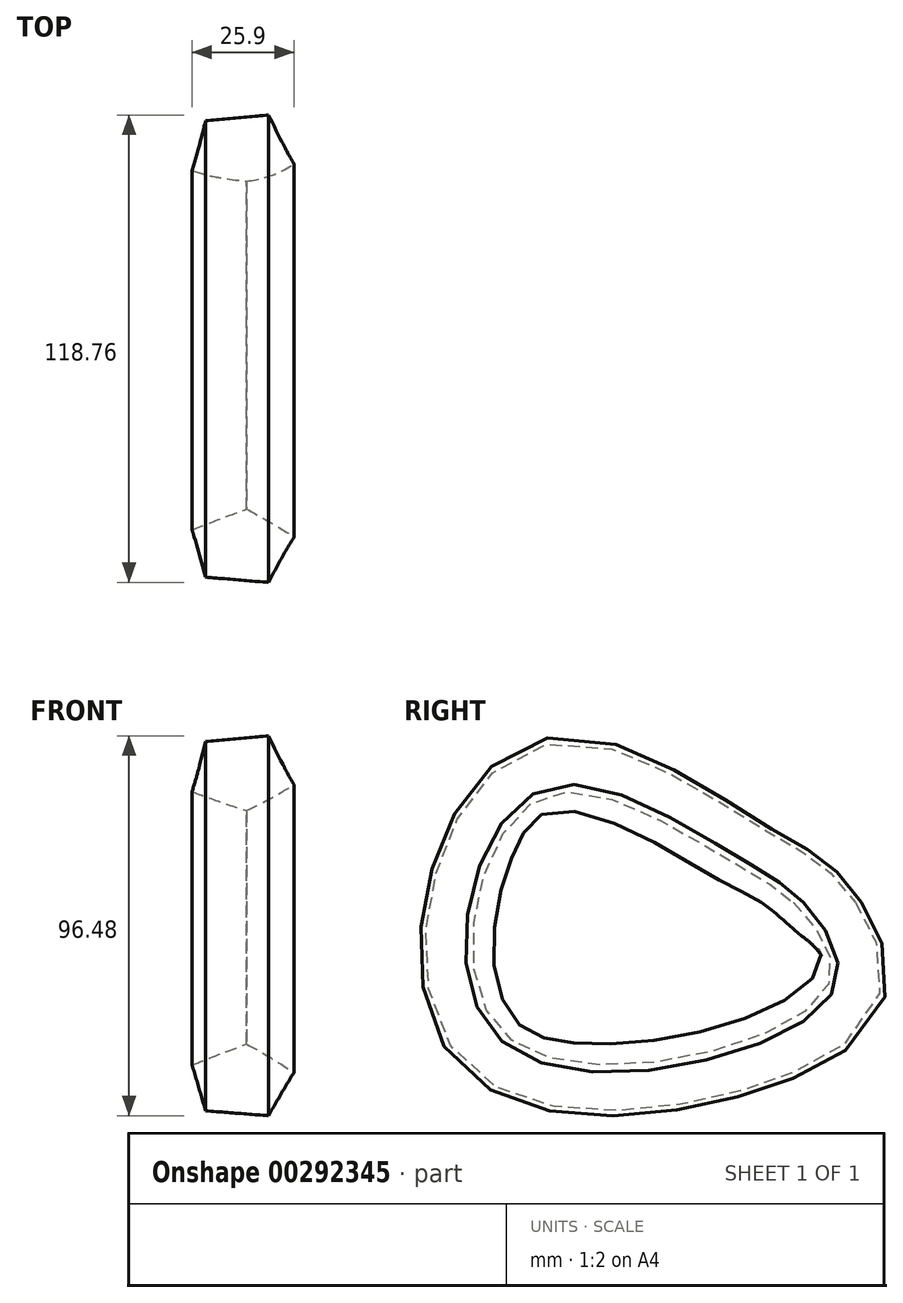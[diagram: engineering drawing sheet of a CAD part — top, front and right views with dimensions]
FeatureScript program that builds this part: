
annotation { "Feature Type Name" : "Feature", "Feature Type Description" : "" }
export const myFeature = defineFeature(function(context is Context, id is Id, definition is map)
    precondition{}
    {
        {
            var Q0;
            Q0=qCreatedBy(makeId("Top.planeOp"),FACE);
            var sketch = newSketch(context, id + "F0", { "sketchPlane" : qUnion([Q0])});
            skLineSegment(sketch, "E0.0", {"start": v(-117.13, 47.21) * mm, "end": v(-131.02, 55.33) * mm});
            skLineSegment(sketch, "E0.1", {"start": v(-131.02, 55.33) * mm, "end": v(-127.6, 71.05) * mm});
            skLineSegment(sketch, "E0.2", {"start": v(-127.6, 71.05) * mm, "end": v(-111.59, 72.65) * mm});
            skLineSegment(sketch, "E0.3", {"start": v(-111.59, 72.65) * mm, "end": v(-105.12, 57.92) * mm});
            skLineSegment(sketch, "E0.4", {"start": v(-105.12, 57.92) * mm, "end": v(-117.13, 47.21) * mm});
            skSolve(sketch);
        }
        {
            var Q0;
            Q0=qCreatedBy(makeId("Right.planeOp"),FACE);
            var sketch = newSketch(context, id + "F1", { "sketchPlane" : qUnion([Q0])});
            skFitSpline(sketch, "E1", {"points": [v(57.66, 0) * mm, v(66.28, -19.52) * mm, v(34.5, -39.5) * mm, v(-17.7, -35.86) * mm, v(-26.79, 0) * mm, v(-5, 29.5) * mm, v(39.04, 12.71) * mm, v(57.66, 0) * mm]});
            skSolve(sketch);
        }
        {
            var Q0;
            Q0 = qSketchRegion(id + "F0", true);
            var Q1;
            Q1 = qConstructionFilter(qBodyType(qCreatedBy(id + "F1" ,EDGE), BodyType.WIRE), ConstructionObject.NO);
            sweep(context, id + "F2", {"profiles" : qUnion([Q0]), "path" : qUnion([Q1])});
        }
    });
